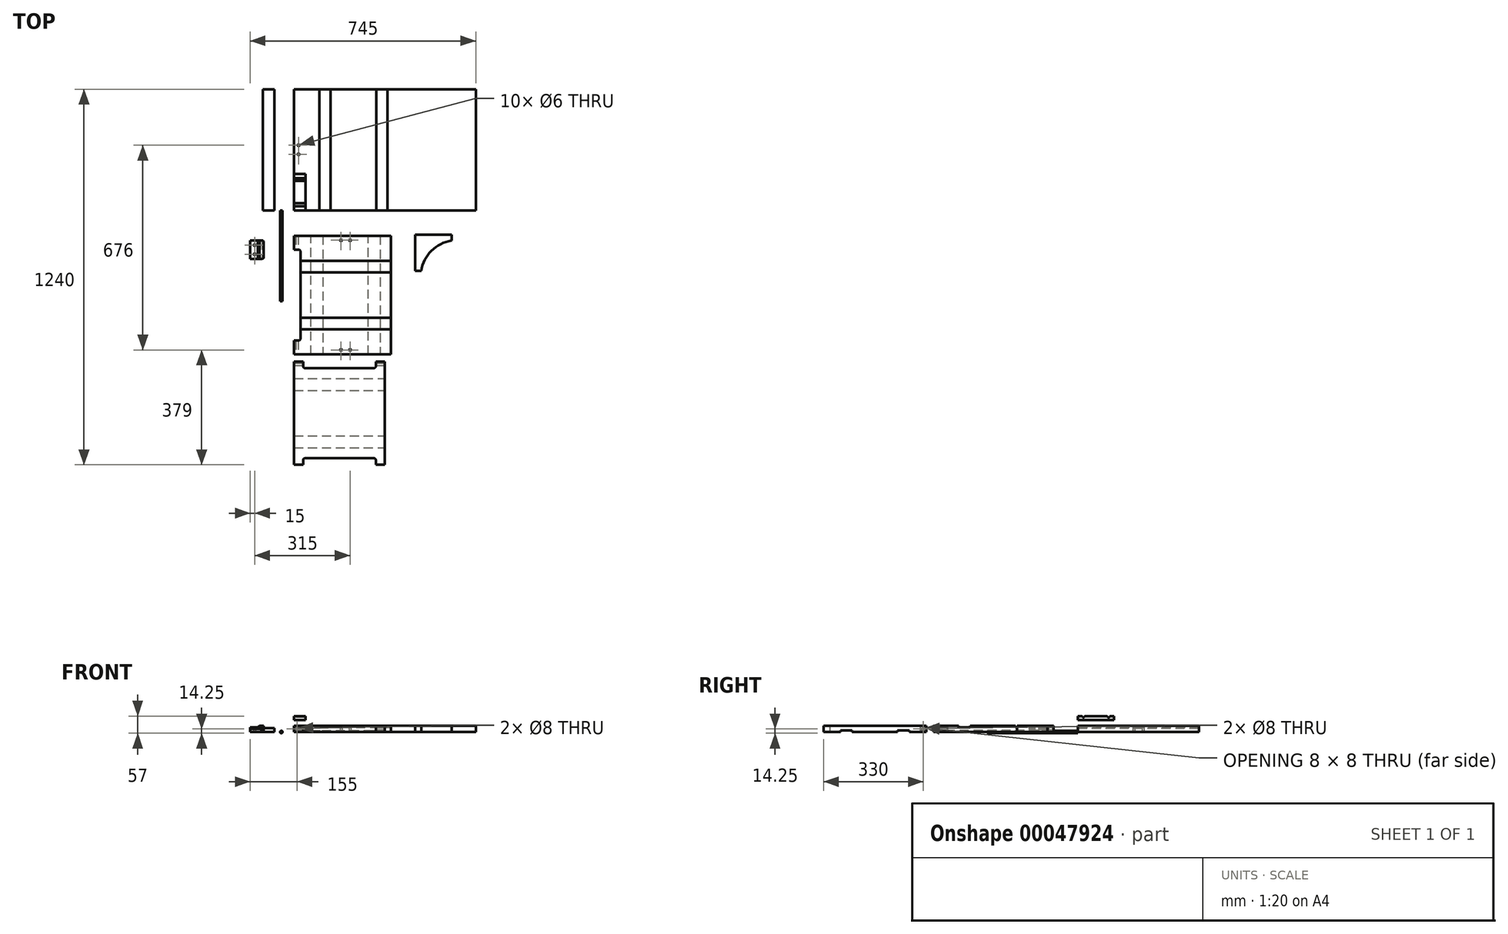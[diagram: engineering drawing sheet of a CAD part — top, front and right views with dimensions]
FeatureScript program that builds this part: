
annotation { "Feature Type Name" : "Feature", "Feature Type Description" : "" }
export const myFeature = defineFeature(function(context is Context, id is Id, definition is map)
    precondition{}
    {
        {
            var Q0;
            Q0=qCreatedBy(makeId("Top.planeOp"),FACE);
            var sketch = newSketch(context, id + "F0", { "sketchPlane" : qUnion([Q0])});
            skLineSegment(sketch, "E0.bottom", {"start": v(0, 0) * mm, "end": v(600, 0) * mm});
            skLineSegment(sketch, "E0.top", {"start": v(0, 400) * mm, "end": v(600, 400) * mm});
            skLineSegment(sketch, "E0.left", {"start": v(0, 0) * mm, "end": v(0, 400) * mm});
            skLineSegment(sketch, "E0.right", {"start": v(600, 0) * mm, "end": v(600, 400) * mm});
            skCircle(sketch, "E1", {"center": v(15, 215) * mm, "radius": 3 * mm});
            skCircle(sketch, "E2", {"center": v(15, 185) * mm, "radius": 3 * mm});
            skLineSegment(sketch, "E3", {"start": v(15, 400) * mm, "end": v(15, 0) * mm, "construction": true});
            skPoint(sketch, "E4", {"position": v(0, 200) * mm});
            skSolve(sketch);
        }
        {
            var Q0;
            Q0=makeQuery(id+"F0.imprint","IMPRINT",FACE,{"disambiguationData":[TD([[makeQuery(id+"F0.imprint","IMPRINT",EDGE,{"derivedFrom":sQuery(id+"F0.wireOp",EDGE,"E0.bottom")}),1.0]])]});
            extrude(context, id + "F1", {"entities" : qUnion([Q0]), "depth" : 20.5 * mm});
        }
        {
            var Q0;
            Q0=makeQuery(id+"F1.opExtrude","CAP_FACE",FACE,{"disambiguationData":[OSD([sQuery(id+"F0.wireOp",EDGE,"E0.bottom"),sQuery(id+"F0.wireOp",EDGE,"E0.top"),sQuery(id+"F0.wireOp",EDGE,"E0.left"),sQuery(id+"F0.wireOp",EDGE,"E0.right"),sQuery(id+"F0.wireOp",EDGE,"E1"),sQuery(id+"F0.wireOp",EDGE,"E2")])],"isStart":false});
            var sketch = newSketch(context, id + "F2", { "sketchPlane" : qUnion([Q0])});
            skLineSegment(sketch, "E5", {"start": v(83, 400) * mm, "end": v(83, 0) * mm});
            skLineSegment(sketch, "E6", {"start": v(83, 0) * mm, "end": v(121, 0) * mm});
            skLineSegment(sketch, "E7", {"start": v(121, 0) * mm, "end": v(121, 400) * mm});
            skLineSegment(sketch, "E8", {"start": v(121, 400) * mm, "end": v(83, 400) * mm});
            skLineSegment(sketch, "E9", {"start": v(271, 400) * mm, "end": v(271, 0) * mm});
            skLineSegment(sketch, "E10", {"start": v(271, 0) * mm, "end": v(309, 0) * mm});
            skLineSegment(sketch, "E11", {"start": v(309, 0) * mm, "end": v(309, 400) * mm});
            skLineSegment(sketch, "E12", {"start": v(309, 400) * mm, "end": v(271, 400) * mm});
            skLineSegment(sketch, "E13", {"start": v(15, 215) * mm, "end": v(15, 185) * mm, "construction": true});
            skSolve(sketch);
        }
        {
            var Q0;
            Q0=makeQuery(id+"F2.imprint","IMPRINT",FACE,{"disambiguationData":[TD([[makeQuery(id+"F2.imprint","IMPRINT",EDGE,{"derivedFrom":sQuery(id+"F2.wireOp",EDGE,"E9")}),1.0]])]});
            var Q1;
            Q1=makeQuery(id+"F2.imprint","IMPRINT",FACE,{"disambiguationData":[TD([[makeQuery(id+"F2.imprint","IMPRINT",EDGE,{"derivedFrom":sQuery(id+"F2.wireOp",EDGE,"E5")}),1.0]])]});
            extrude(context, id + "F3", {"entities" : qUnion([Q0, Q1]), "operationType" : NewBodyOperationType.REMOVE, "oppositeDirection" : true, "depth" : 6 * mm});
        }
        {
            var Q0;
            Q0=qCreatedBy(makeId("Top.planeOp"),FACE);
            var sketch = newSketch(context, id + "F4", { "sketchPlane" : qUnion([Q0])});
            skLineSegment(sketch, "E14.bottom", {"start": v(-65.23, 0) * mm, "end": v(-103.23, 0) * mm});
            skLineSegment(sketch, "E14.top", {"start": v(-65.23, 400) * mm, "end": v(-103.23, 400) * mm});
            skLineSegment(sketch, "E14.left", {"start": v(-65.23, 0) * mm, "end": v(-65.23, 400) * mm});
            skLineSegment(sketch, "E14.right", {"start": v(-103.23, 0) * mm, "end": v(-103.23, 400) * mm});
            skSolve(sketch);
        }
        {
            var Q0;
            Q0=makeQuery(id+"F4.imprint","IMPRINT",FACE,{"disambiguationData":[TD([[makeQuery(id+"F4.imprint","IMPRINT",EDGE,{"derivedFrom":sQuery(id+"F4.wireOp",EDGE,"E14.bottom")}),-1.0]])]});
            extrude(context, id + "F5", {"entities" : qUnion([Q0]), "depth" : 13 * mm});
        }
        {
            var Q0;
            Q0=qCreatedBy(makeId("Top.planeOp"),FACE);
            var sketch = newSketch(context, id + "F6", { "sketchPlane" : qUnion([Q0])});
            skLineSegment(sketch, "E15.bottom", {"start": v(0, -84) * mm, "end": v(320, -84) * mm});
            skLineSegment(sketch, "E15.top", {"start": v(0, -476) * mm, "end": v(320, -476) * mm});
            skLineSegment(sketch, "E15.left", {"start": v(0, -84) * mm, "end": v(0, -476) * mm});
            skLineSegment(sketch, "E15.right", {"start": v(320, -84) * mm, "end": v(320, -476) * mm});
            skLineSegment(sketch, "E16", {"start": v(0, -130) * mm, "end": v(15, -130) * mm});
            skArc(sketch, "E17", {"start": v(15, -130) * mm, "mid": v(19.24, -131.76) * mm, "end": v(21, -136) * mm});
            skLineSegment(sketch, "E18", {"start": v(21, -136) * mm, "end": v(21, -424) * mm});
            skArc(sketch, "E19", {"start": v(21, -424) * mm, "mid": v(19.24, -428.24) * mm, "end": v(15, -430) * mm});
            skLineSegment(sketch, "E20", {"start": v(15, -430) * mm, "end": v(0, -430) * mm});
            skCircle(sketch, "E21", {"center": v(155, -99) * mm, "radius": 3 * mm});
            skCircle(sketch, "E22", {"center": v(185, -99) * mm, "radius": 3 * mm});
            skCircle(sketch, "E23", {"center": v(155, -461) * mm, "radius": 3 * mm});
            skCircle(sketch, "E24", {"center": v(185, -461) * mm, "radius": 3 * mm});
            skSolve(sketch);
        }
        {
            var Q0;
            {var subQ2=sQuery(id+"F6.wireOp",EDGE,"E15.bottom");Q0=makeQuery(id+"F6.imprint","IMPRINT",FACE,{"disambiguationData":[TD([[makeQuery(id+"F6.imprint","IMPRINT",EDGE,{"derivedFrom":subQ2}),-1.0]])]});}
            extrude(context, id + "F7", {"entities" : qUnion([Q0]), "depth" : 20.5 * mm});
        }
        {
            var Q0;
            Q0=makeQuery(id+"F7.opExtrude","CAP_FACE",FACE,{"disambiguationData":[OSD([sQuery(id+"F6.wireOp",EDGE,"E15.bottom"),sQuery(id+"F6.wireOp",EDGE,"E15.top"),sQuery(id+"F6.wireOp",EDGE,"E15.left"),sQuery(id+"F6.wireOp",EDGE,"E15.right"),sQuery(id+"F6.wireOp",EDGE,"E16"),sQuery(id+"F6.wireOp",EDGE,"E17"),sQuery(id+"F6.wireOp",EDGE,"E18"),sQuery(id+"F6.wireOp",EDGE,"E19"),sQuery(id+"F6.wireOp",EDGE,"E20")])],"isStart":true});
            var sketch = newSketch(context, id + "F8", { "sketchPlane" : qUnion([Q0])});
            skLineSegment(sketch, "E25", {"start": v(284, 84) * mm, "end": v(284, 476) * mm});
            skLineSegment(sketch, "E26", {"start": v(284, 476) * mm, "end": v(245, 476) * mm});
            skLineSegment(sketch, "E27", {"start": v(245, 476) * mm, "end": v(245, 84) * mm});
            skLineSegment(sketch, "E28", {"start": v(245, 84) * mm, "end": v(284, 84) * mm});
            skLineSegment(sketch, "E29", {"start": v(95, 84) * mm, "end": v(95, 476) * mm});
            skLineSegment(sketch, "E30", {"start": v(95, 476) * mm, "end": v(56, 476) * mm});
            skLineSegment(sketch, "E31", {"start": v(56, 476) * mm, "end": v(56, 84) * mm});
            skLineSegment(sketch, "E32", {"start": v(56, 84) * mm, "end": v(95, 84) * mm});
            skLineSegment(sketch, "E33", {"start": v(155, 99) * mm, "end": v(185, 99) * mm, "construction": true});
            skPoint(sketch, "E34", {"position": v(170, 99) * mm});
            skSolve(sketch);
        }
        {
            var Q0;
            Q0=makeQuery(id+"F8.imprint","IMPRINT",FACE,{"disambiguationData":[TD([[makeQuery(id+"F8.imprint","IMPRINT",EDGE,{"derivedFrom":sQuery(id+"F8.wireOp",EDGE,"E25")}),1.0]])]});
            var Q1;
            Q1=makeQuery(id+"F8.imprint","IMPRINT",FACE,{"disambiguationData":[TD([[makeQuery(id+"F8.imprint","IMPRINT",EDGE,{"derivedFrom":sQuery(id+"F8.wireOp",EDGE,"E29")}),1.0]])]});
            extrude(context, id + "F9", {"entities" : qUnion([Q0, Q1]), "operationType" : NewBodyOperationType.REMOVE, "oppositeDirection" : true, "depth" : 5 * mm});
        }
        {
            var Q0;
            Q0=makeQuery(id+"F7.opExtrude","CAP_FACE",FACE,{"disambiguationData":[OSD([sQuery(id+"F6.wireOp",EDGE,"E15.bottom"),sQuery(id+"F6.wireOp",EDGE,"E15.top"),sQuery(id+"F6.wireOp",EDGE,"E15.left"),sQuery(id+"F6.wireOp",EDGE,"E15.right"),sQuery(id+"F6.wireOp",EDGE,"E16"),sQuery(id+"F6.wireOp",EDGE,"E17"),sQuery(id+"F6.wireOp",EDGE,"E18"),sQuery(id+"F6.wireOp",EDGE,"E19"),sQuery(id+"F6.wireOp",EDGE,"E20")])],"isStart":false});
            var sketch = newSketch(context, id + "F10", { "sketchPlane" : qUnion([Q0])});
            skLineSegment(sketch, "E35.bottom", {"start": v(21, -205) * mm, "end": v(320, -205) * mm});
            skLineSegment(sketch, "E35.top", {"start": v(21, -167) * mm, "end": v(320, -167) * mm});
            skLineSegment(sketch, "E35.left", {"start": v(21, -205) * mm, "end": v(21, -167) * mm});
            skLineSegment(sketch, "E35.right", {"start": v(320, -205) * mm, "end": v(320, -167) * mm});
            skLineSegment(sketch, "E36.bottom", {"start": v(21, -393) * mm, "end": v(320, -393) * mm});
            skLineSegment(sketch, "E36.top", {"start": v(21, -355) * mm, "end": v(320, -355) * mm});
            skLineSegment(sketch, "E36.left", {"start": v(21, -393) * mm, "end": v(21, -355) * mm});
            skLineSegment(sketch, "E36.right", {"start": v(320, -393) * mm, "end": v(320, -355) * mm});
            skLineSegment(sketch, "E37", {"start": v(155, -99) * mm, "end": v(185, -99) * mm, "construction": true});
            skLineSegment(sketch, "E38", {"start": v(155, -461) * mm, "end": v(185, -461) * mm, "construction": true});
            skSolve(sketch);
        }
        {
            var Q0;
            Q0=makeQuery(id+"F10.imprint","IMPRINT",FACE,{"disambiguationData":[TD([[makeQuery(id+"F10.imprint","IMPRINT",EDGE,{"derivedFrom":sQuery(id+"F10.wireOp",EDGE,"E35.bottom")}),1.0]])]});
            var Q1;
            Q1=makeQuery(id+"F10.imprint","IMPRINT",FACE,{"disambiguationData":[TD([[makeQuery(id+"F10.imprint","IMPRINT",EDGE,{"derivedFrom":sQuery(id+"F10.wireOp",EDGE,"E36.bottom")}),1.0]])]});
            extrude(context, id + "F11", {"entities" : qUnion([Q0, Q1]), "operationType" : NewBodyOperationType.REMOVE, "oppositeDirection" : true, "depth" : 5 * mm});
        }
        {
            var Q0;
            Q0=qCreatedBy(makeId("Top.planeOp"),FACE);
            var sketch = newSketch(context, id + "F12", { "sketchPlane" : qUnion([Q0])});
            skLineSegment(sketch, "E39.bottom", {"start": v(0, -500) * mm, "end": v(300, -500) * mm});
            skLineSegment(sketch, "E39.top", {"start": v(0, -840) * mm, "end": v(300, -840) * mm});
            skLineSegment(sketch, "E39.left", {"start": v(0, -500) * mm, "end": v(0, -840) * mm});
            skLineSegment(sketch, "E39.right", {"start": v(300, -500) * mm, "end": v(300, -840) * mm});
            skLineSegment(sketch, "E40", {"start": v(30, -500) * mm, "end": v(30, -515) * mm});
            skArc(sketch, "E41", {"start": v(30, -515) * mm, "mid": v(31.76, -519.24) * mm, "end": v(36, -521) * mm});
            skLineSegment(sketch, "E42", {"start": v(36, -521) * mm, "end": v(264, -521) * mm});
            skArc(sketch, "E43", {"start": v(264, -521) * mm, "mid": v(268.24, -519.24) * mm, "end": v(270, -515) * mm});
            skLineSegment(sketch, "E44", {"start": v(270, -515) * mm, "end": v(270, -500) * mm});
            skLineSegment(sketch, "E45", {"start": v(30, -840) * mm, "end": v(30, -825) * mm});
            skArc(sketch, "E46", {"start": v(30, -825) * mm, "mid": v(31.76, -820.76) * mm, "end": v(36, -819) * mm});
            skLineSegment(sketch, "E47", {"start": v(36, -819) * mm, "end": v(264, -819) * mm});
            skArc(sketch, "E48", {"start": v(264, -819) * mm, "mid": v(268.24, -820.76) * mm, "end": v(270, -825) * mm});
            skLineSegment(sketch, "E49", {"start": v(270, -825) * mm, "end": v(270, -840) * mm});
            skSolve(sketch);
        }
        {
            var Q0;
            Q0=makeQuery(id+"F12.imprint","IMPRINT",FACE,{"disambiguationData":[TD([[makeQuery(id+"F12.imprint","IMPRINT",EDGE,{"derivedFrom":sQuery(id+"F12.wireOp",EDGE,"E39.bottom")}),-1.0]])]});
            extrude(context, id + "F13", {"entities" : qUnion([Q0]), "depth" : 20.5 * mm});
        }
        {
            var Q0;
            Q0=makeQuery(id+"F13.opExtrude","CAP_FACE",FACE,{"disambiguationData":[OSD([sQuery(id+"F12.wireOp",EDGE,"E39.bottom"),sQuery(id+"F12.wireOp",EDGE,"E39.top"),sQuery(id+"F12.wireOp",EDGE,"E39.left"),sQuery(id+"F12.wireOp",EDGE,"E39.right")])],"isStart":true});
            var sketch = newSketch(context, id + "F14", { "sketchPlane" : qUnion([Q0])});
            skLineSegment(sketch, "E50.bottom", {"start": v(0, 784) * mm, "end": v(300, 784) * mm});
            skLineSegment(sketch, "E50.top", {"start": v(0, 745) * mm, "end": v(300, 745) * mm});
            skLineSegment(sketch, "E50.left", {"start": v(0, 784) * mm, "end": v(0, 745) * mm});
            skLineSegment(sketch, "E50.right", {"start": v(300, 784) * mm, "end": v(300, 745) * mm});
            skLineSegment(sketch, "E51.bottom", {"start": v(0, 595) * mm, "end": v(300, 595) * mm});
            skLineSegment(sketch, "E51.top", {"start": v(0, 556) * mm, "end": v(300, 556) * mm});
            skLineSegment(sketch, "E51.left", {"start": v(0, 595) * mm, "end": v(0, 556) * mm});
            skLineSegment(sketch, "E51.right", {"start": v(300, 595) * mm, "end": v(300, 556) * mm});
            skPoint(sketch, "E52", {"position": v(300, 670) * mm});
            skSolve(sketch);
        }
        {
            var Q0;
            Q0=makeQuery(id+"F14.imprint","IMPRINT",FACE,{"disambiguationData":[TD([[makeQuery(id+"F14.imprint","IMPRINT",EDGE,{"derivedFrom":sQuery(id+"F14.wireOp",EDGE,"E50.bottom")}),-1.0]])]});
            var Q1;
            Q1=makeQuery(id+"F14.imprint","IMPRINT",FACE,{"disambiguationData":[TD([[makeQuery(id+"F14.imprint","IMPRINT",EDGE,{"derivedFrom":sQuery(id+"F14.wireOp",EDGE,"E51.bottom")}),-1.0]])]});
            extrude(context, id + "F15", {"entities" : qUnion([Q0, Q1]), "operationType" : NewBodyOperationType.REMOVE, "oppositeDirection" : true, "depth" : 5 * mm});
        }
        {
            var Q0;
            Q0=makeQuery(id+"F7.opExtrude","SWEPT_FACE",FACE,{"disambiguationData":[OSD([sQuery(id+"F6.wireOp",EDGE,"E15.top")])]});
            var sketch = newSketch(context, id + "F16", { "sketchPlane" : qUnion([Q0])});
            skCircle(sketch, "E53", {"center": v(10, 10.25) * mm, "radius": 4 * mm});
            skPoint(sketch, "E53.centerSnap0", {"position": v(0, 10.25) * mm});
            skSolve(sketch);
        }
        {
            var Q0;
            Q0=makeQuery(id+"F16.imprint","IMPRINT",FACE,{"disambiguationData":[TD([[makeQuery(id+"F16.imprint","IMPRINT",EDGE,{"derivedFrom":sQuery(id+"F16.wireOp",EDGE,"E53")}),1.0]])]});
            var Q1;
            Q1=makeQuery(id+"F7.opExtrude","SWEPT_FACE",FACE,{"disambiguationData":[OSD([sQuery(id+"F6.wireOp",EDGE,"E15.bottom")])]});
            extrude(context, id + "F17", {"entities" : qUnion([Q0]), "operationType" : NewBodyOperationType.REMOVE, "endBound" : BoundingType.UP_TO_SURFACE, "oppositeDirection" : true, "endBoundEntityFace" : qUnion([Q1]), "depth" : 25 * mm});
        }
        {
            var Q0;
            Q0=qCreatedBy(makeId("Top.planeOp"),FACE);
            var sketch = newSketch(context, id + "F18", { "sketchPlane" : qUnion([Q0])});
            skLineSegment(sketch, "E54.bottom", {"start": v(-105, -100) * mm, "end": v(-145, -100) * mm});
            skLineSegment(sketch, "E54.top", {"start": v(-105, -160) * mm, "end": v(-145, -160) * mm});
            skLineSegment(sketch, "E54.left", {"start": v(-100, -105) * mm, "end": v(-100, -155) * mm});
            skLineSegment(sketch, "E54.right", {"start": v(-145, -100) * mm, "end": v(-145, -160) * mm});
            skCircle(sketch, "E55", {"center": v(-130, -115) * mm, "radius": 3 * mm});
            skCircle(sketch, "E56", {"center": v(-130, -145) * mm, "radius": 3 * mm});
            skPoint(sketch, "E57.visualSharp", {"position": v(-100, -100) * mm});
            skArc(sketch, "E57.filletArc", {"start": v(-100, -105) * mm, "mid": v(-101.46, -101.46) * mm, "end": v(-105, -100) * mm});
            skPoint(sketch, "E58.visualSharp", {"position": v(-100, -160) * mm});
            skArc(sketch, "E58.filletArc", {"start": v(-105, -160) * mm, "mid": v(-101.46, -158.54) * mm, "end": v(-100, -155) * mm});
            skSolve(sketch);
        }
        {
            var Q0;
            Q0=makeQuery(id+"F18.imprint","IMPRINT",FACE,{"disambiguationData":[TD([[makeQuery(id+"F18.imprint","IMPRINT",EDGE,{"derivedFrom":sQuery(id+"F18.wireOp",EDGE,"E54.bottom")}),1.0]])]});
            extrude(context, id + "F19", {"entities" : qUnion([Q0]), "depth" : 20.5 * mm});
        }
        {
            var Q0;
            Q0=makeQuery(id+"F19.opExtrude","SWEPT_FACE",FACE,{"disambiguationData":[OSD([sQuery(id+"F18.wireOp",EDGE,"E54.top")])]});
            var sketch = newSketch(context, id + "F20", { "sketchPlane" : qUnion([Q0])});
            skLineSegment(sketch, "E59", {"start": v(-145, 11) * mm, "end": v(-112.87, 11) * mm});
            skArc(sketch, "E60", {"start": v(-112.46, 10) * mm, "mid": v(-105.3, 13.51) * mm, "end": v(-112.87, 11) * mm});
            skLineSegment(sketch, "E61", {"start": v(-112.46, 10) * mm, "end": v(-145, 10) * mm});
            skLineSegment(sketch, "E62", {"start": v(-145, 10) * mm, "end": v(-145, 11) * mm});
            skLineSegment(sketch, "E63", {"start": v(-145, 20.5) * mm, "end": v(-145, 16) * mm});
            skLineSegment(sketch, "E64", {"start": v(-145, 16) * mm, "end": v(-119, 16) * mm});
            skLineSegment(sketch, "E65", {"start": v(-119, 16) * mm, "end": v(-114, 20.5) * mm});
            skLineSegment(sketch, "E66", {"start": v(-114, 20.5) * mm, "end": v(-145, 20.5) * mm});
            skSolve(sketch);
        }
        {
            var Q0;
            Q0=makeQuery(id+"F20.imprint","IMPRINT",FACE,{"disambiguationData":[TD([[makeQuery(id+"F20.imprint","IMPRINT",EDGE,{"derivedFrom":sQuery(id+"F20.wireOp",EDGE,"E59")}),-1.0]])]});
            var Q1;
            Q1=makeQuery(id+"F20.imprint","IMPRINT",FACE,{"disambiguationData":[TD([[makeQuery(id+"F20.imprint","IMPRINT",EDGE,{"derivedFrom":sQuery(id+"F20.wireOp",EDGE,"E63")}),1.0]])]});
            var Q2;
            Q2=makeQuery(id+"F19.opExtrude","SWEPT_FACE",FACE,{"disambiguationData":[OSD([sQuery(id+"F18.wireOp",EDGE,"E54.bottom")])]});
            extrude(context, id + "F21", {"entities" : qUnion([Q0, Q1]), "operationType" : NewBodyOperationType.REMOVE, "endBound" : BoundingType.UP_TO_SURFACE, "oppositeDirection" : true, "endBoundEntityFace" : qUnion([Q2]), "depth" : 25 * mm});
        }
        {
            var Q0;
            Q0=makeQuery(id+"F13.opExtrude","SWEPT_FACE",FACE,{"disambiguationData":[OSD([sQuery(id+"F12.wireOp",EDGE,"E39.left")])]});
            var sketch = newSketch(context, id + "F22", { "sketchPlane" : qUnion([Q0])});
            skCircle(sketch, "E67", {"center": v(510, 10.25) * mm, "radius": 4 * mm});
            skPoint(sketch, "E67.centerSnap0", {"position": v(500, 10.25) * mm});
            skSolve(sketch);
        }
        {
            var Q0;
            Q0=makeQuery(id+"F22.imprint","IMPRINT",FACE,{"disambiguationData":[TD([[makeQuery(id+"F22.imprint","IMPRINT",EDGE,{"derivedFrom":sQuery(id+"F22.wireOp",EDGE,"E67")}),1.0]])]});
            var Q1;
            Q1=makeQuery(id+"F13.opExtrude","SWEPT_FACE",FACE,{"disambiguationData":[OSD([sQuery(id+"F12.wireOp",EDGE,"E39.right")])]});
            extrude(context, id + "F23", {"entities" : qUnion([Q0]), "operationType" : NewBodyOperationType.REMOVE, "endBound" : BoundingType.UP_TO_SURFACE, "oppositeDirection" : true, "endBoundEntityFace" : qUnion([Q1]), "depth" : 25 * mm});
        }
        {
            var Q0;
            Q0=qCreatedBy(makeId("Front.planeOp"),FACE);
            var sketch = newSketch(context, id + "F24", { "sketchPlane" : qUnion([Q0])});
            skCircle(sketch, "E68", {"center": v(-42, 0) * mm, "radius": 4 * mm});
            skSolve(sketch);
        }
        {
            var Q0;
            Q0=makeQuery(id+"F24.imprint","IMPRINT",FACE,{"disambiguationData":[TD([[makeQuery(id+"F24.imprint","IMPRINT",EDGE,{"derivedFrom":sQuery(id+"F24.wireOp",EDGE,"E68")}),1.0]])]});
            extrude(context, id + "F25", {"entities" : qUnion([Q0]), "depth" : 300 * mm});
        }
        {
            var Q0;
            Q0=qCreatedBy(makeId("Top.planeOp"),FACE);
            var sketch = newSketch(context, id + "F26", { "sketchPlane" : qUnion([Q0])});
            skLineSegment(sketch, "E69", {"start": v(400, -80) * mm, "end": v(400, -200) * mm});
            skLineSegment(sketch, "E70", {"start": v(400, -200) * mm, "end": v(420, -200) * mm});
            skLineSegment(sketch, "E71", {"start": v(420, -200) * mm, "end": v(520, -100) * mm, "construction": true});
            skLineSegment(sketch, "E72", {"start": v(520, -100) * mm, "end": v(520, -80) * mm});
            skLineSegment(sketch, "E73", {"start": v(520, -80) * mm, "end": v(400, -80) * mm});
            skArc(sketch, "E74", {"start": v(520, -100) * mm, "mid": v(453.7, -133.7) * mm, "end": v(420, -200) * mm});
            skSolve(sketch);
        }
        {
            var Q0;
            Q0 = qSketchRegion(id + "F26", true);
            extrude(context, id + "F27", {"entities" : qUnion([Q0]), "depth" : 20.5 * mm});
        }
        {
            var Q0;
            Q0=qCreatedBy(makeId("Right.planeOp"),FACE);
            var sketch = newSketch(context, id + "F28", { "sketchPlane" : qUnion([Q0])});
            skLineSegment(sketch, "E75", {"start": v(0, 40) * mm, "end": v(120, 40) * mm});
            skLineSegment(sketch, "E76", {"start": v(120, 40) * mm, "end": v(120, 53) * mm});
            skLineSegment(sketch, "E77", {"start": v(120, 53) * mm, "end": v(106, 53) * mm});
            skArc(sketch, "E78", {"start": v(97, 53) * mm, "mid": v(101.5, 48.5) * mm, "end": v(106, 53) * mm});
            skLineSegment(sketch, "E79", {"start": v(97, 53) * mm, "end": v(23, 53) * mm});
            skArc(sketch, "E80", {"start": v(14, 53) * mm, "mid": v(18.5, 48.5) * mm, "end": v(23, 53) * mm});
            skLineSegment(sketch, "E81", {"start": v(14, 53) * mm, "end": v(0, 53) * mm});
            skLineSegment(sketch, "E82", {"start": v(0, 53) * mm, "end": v(0, 40) * mm});
            skSolve(sketch);
        }
        {
            var Q0;
            Q0=makeQuery(id+"F28.imprint","IMPRINT",FACE,{"disambiguationData":[TD([[makeQuery(id+"F28.imprint","IMPRINT",EDGE,{"derivedFrom":sQuery(id+"F28.wireOp",EDGE,"E75")}),1.0]])]});
            extrude(context, id + "F29", {"entities" : qUnion([Q0]), "depth" : 38 * mm});
        }
    });
